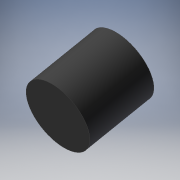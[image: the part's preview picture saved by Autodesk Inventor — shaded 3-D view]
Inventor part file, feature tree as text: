
AUTODESK INVENTOR PART (.ipt)
format: ipt  version: 2019 (Build 230136000, 136)  size: 108,544 bytes
history: native  units: mm
features: extrude x1, sketch x1
ambient origin geometry x8: Origin, YZ Plane, XZ Plane, XY Plane, X Axis, Y Axis, Z Axis, Center Point
bodies: Solid1 (feature_tree)
feature tree (2):
  extrude  "Extrusion1"  [1 undecoded]
  sketch  "Sketch_1"  dims[d0=1.67mm d1=0.0mm]
note: 1 required parameter value undecoded (feature->parameter linkage not recoverable at this tier; creation-order binding heuristic only, values carry confidence <= 0.55)
